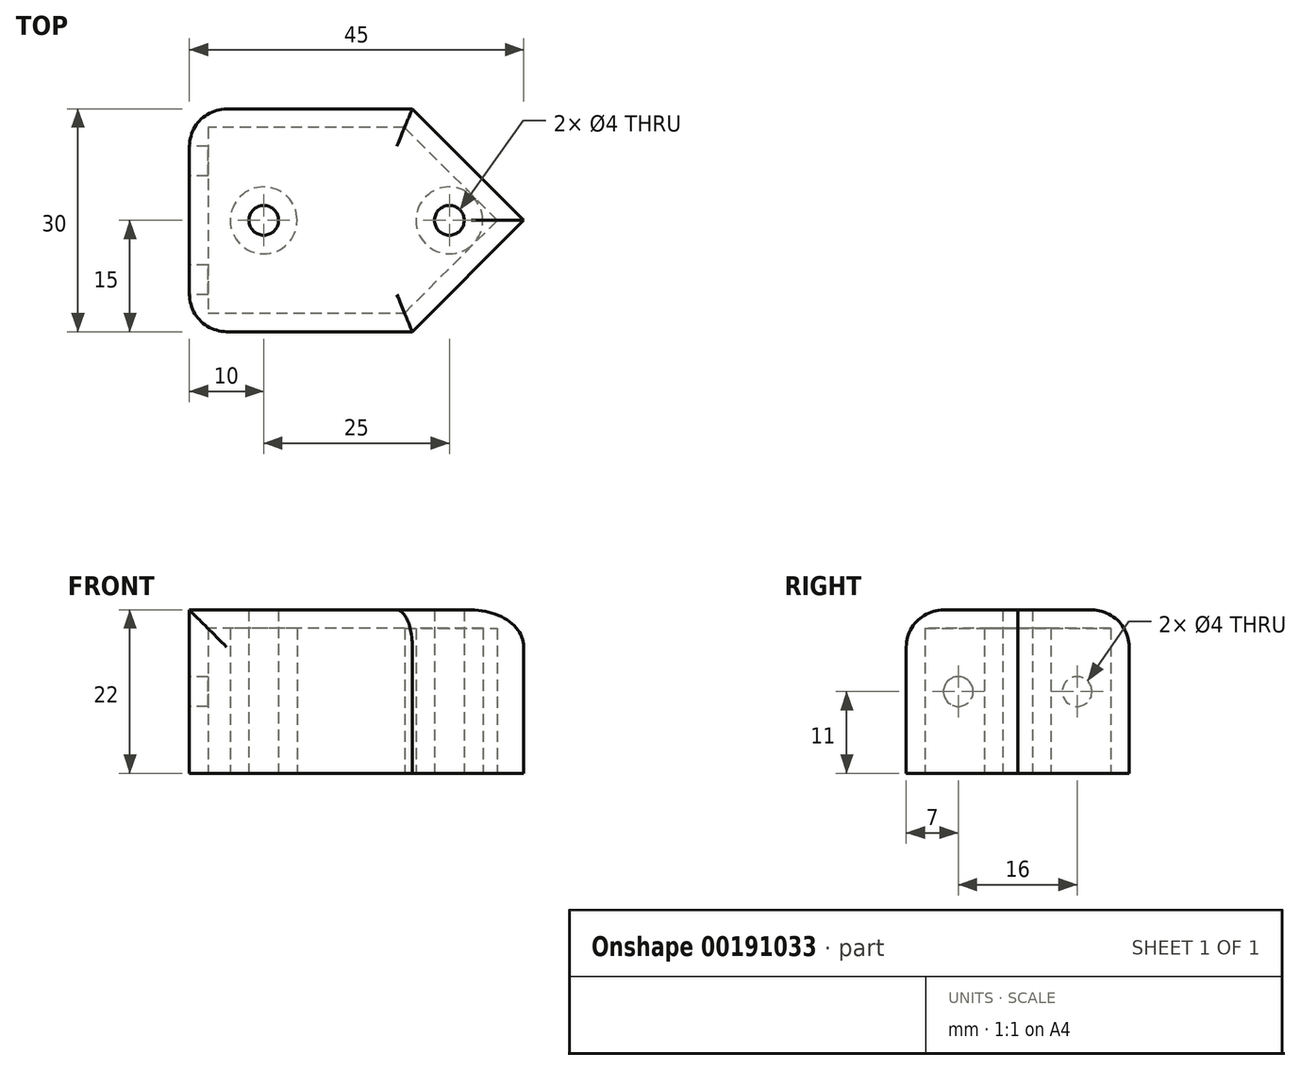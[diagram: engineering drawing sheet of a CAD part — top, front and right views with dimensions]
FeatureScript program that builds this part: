
annotation { "Feature Type Name" : "Feature", "Feature Type Description" : "" }
export const myFeature = defineFeature(function(context is Context, id is Id, definition is map)
    precondition{}
    {
        {
            var Q0;
            Q0=qCreatedBy(makeId("Top.planeOp"),FACE);
            var sketch = newSketch(context, id + "F0", { "sketchPlane" : qUnion([Q0])});
            skLineSegment(sketch, "E0", {"start": v(0, 0) * mm, "end": v(-15, 15) * mm});
            skLineSegment(sketch, "E1", {"start": v(-15, 15) * mm, "end": v(-45, 15) * mm});
            skLineSegment(sketch, "E2", {"start": v(-45, 15) * mm, "end": v(-45, -15) * mm});
            skLineSegment(sketch, "E3", {"start": v(-45, -15) * mm, "end": v(-15, -15) * mm});
            skLineSegment(sketch, "E4", {"start": v(-15, -15) * mm, "end": v(0, 0) * mm});
            skLineSegment(sketch, "E5", {"start": v(-45, 0) * mm, "end": v(0, 0) * mm, "construction": true});
            skLineSegment(sketch, "E6", {"start": v(-30, 15) * mm, "end": v(-30, -15) * mm, "construction": true});
            skPoint(sketch, "E7", {"position": v(-35, 0) * mm});
            skPoint(sketch, "E8", {"position": v(-10, 0) * mm});
            skSolve(sketch);
        }
        {
            var Q0;
            Q0=makeQuery(id+"F0.imprint","IMPRINT",FACE,{"disambiguationData":[TD([[makeQuery(id+"F0.imprint","IMPRINT",EDGE,{"derivedFrom":sQuery(id+"F0.wireOp",EDGE,"E0")}),1.0]])]});
            extrude(context, id + "F1", {"entities" : qUnion([Q0]), "depth" : 22 * mm});
        }
        {
            var Q0;
            Q0=sQuery(id+"F0.wireOp",VERTEX,"E7");
            var Q1;
            Q1=sQuery(id+"F0.wireOp",VERTEX,"E8");
            var Q2;
            Q2=makeQuery(id+"F1.opExtrude","SWEPT_BODY",BODY,{"disambiguationData":[OSD([sQuery(id+"F0.wireOp",EDGE,"E0"),sQuery(id+"F0.wireOp",EDGE,"E1"),sQuery(id+"F0.wireOp",EDGE,"E2"),sQuery(id+"F0.wireOp",EDGE,"E3"),sQuery(id+"F0.wireOp",EDGE,"E4")])]});
            hole(context, id + "F2", {"style" : HoleStyle.SIMPLE, "endStyle" : HoleEndStyle.THROUGH, "oppositeDirection" : true, "holeDiameter" : 4 * mm, "locations" : qUnion([Q0, Q1]), "scope" : qUnion([Q2]), "isTappedThrough" : true});
        }
        {
            var Q0;
            Q0=makeQuery(id+"F1.opExtrude","CAP_FACE",FACE,{"disambiguationData":[OSD([sQuery(id+"F0.wireOp",EDGE,"E0"),sQuery(id+"F0.wireOp",EDGE,"E1"),sQuery(id+"F0.wireOp",EDGE,"E2"),sQuery(id+"F0.wireOp",EDGE,"E3"),sQuery(id+"F0.wireOp",EDGE,"E4")])],"isStart":true});
            shell(context, id + "F3", {"entities" : qUnion([Q0]), "thickness" : 2.5 * mm});
        }
        {
            var Q0;
            Q0=makeQuery(id+"F1.opExtrude","SWEPT_FACE",FACE,{"disambiguationData":[OSD([sQuery(id+"F0.wireOp",EDGE,"E2")])]});
            var sketch = newSketch(context, id + "F4", { "sketchPlane" : qUnion([Q0])});
            skLineSegment(sketch, "E9", {"start": v(0, 22) * mm, "end": v(0, 0) * mm, "construction": true});
            skLineSegment(sketch, "E10", {"start": v(-15, 11) * mm, "end": v(15, 11) * mm, "construction": true});
            skPoint(sketch, "E11", {"position": v(-8, 11) * mm});
            skPoint(sketch, "E12.MirrorP", {"position": v(8, 11) * mm});
            skLineSegment(sketch, "E13.bottom", {"start": v(-15, 22) * mm, "end": v(15, 22) * mm});
            skLineSegment(sketch, "E13.top", {"start": v(-15, 0) * mm, "end": v(15, 0) * mm});
            skLineSegment(sketch, "E13.left", {"start": v(-15, 22) * mm, "end": v(-15, 0) * mm});
            skLineSegment(sketch, "E13.right", {"start": v(15, 22) * mm, "end": v(15, 0) * mm});
            skSolve(sketch);
        }
        {
            var Q0;
            Q0=sQuery(id+"F4.wireOp",VERTEX,"E11");
            var Q1;
            Q1=sQuery(id+"F4.wireOp",VERTEX,"E12.MirrorP");
            var Q2;
            Q2=makeQuery(id+"F1.opExtrude","SWEPT_BODY",BODY,{"disambiguationData":[OSD([sQuery(id+"F0.wireOp",EDGE,"E0"),sQuery(id+"F0.wireOp",EDGE,"E1"),sQuery(id+"F0.wireOp",EDGE,"E2"),sQuery(id+"F0.wireOp",EDGE,"E3"),sQuery(id+"F0.wireOp",EDGE,"E4")])]});
            hole(context, id + "F5", {"style" : HoleStyle.SIMPLE, "endStyle" : HoleEndStyle.BLIND, "holeDiameter" : 4 * mm, "holeDepth" : 6 * mm, "locations" : qUnion([Q0, Q1]), "scope" : qUnion([Q2])});
        }
        {
            var Q0;
            Q0=makeQuery(id+"F1.opExtrude","CAP_EDGE",EDGE,{"disambiguationData":[OSD([sQuery(id+"F0.wireOp",EDGE,"E3")])],"isStart":false});
            var Q1;
            Q1=makeQuery(id+"F1.opExtrude","CAP_EDGE",EDGE,{"disambiguationData":[OSD([sQuery(id+"F0.wireOp",EDGE,"E4")])],"isStart":false});
            var Q2;
            Q2=makeQuery(id+"F1.opExtrude","CAP_EDGE",EDGE,{"disambiguationData":[OSD([sQuery(id+"F0.wireOp",EDGE,"E0")])],"isStart":false});
            var Q3;
            Q3=makeQuery(id+"F1.opExtrude","CAP_EDGE",EDGE,{"disambiguationData":[OSD([sQuery(id+"F0.wireOp",EDGE,"E1")])],"isStart":false});
            var Q4;
            Q4=makeQuery(id+"F1.opExtrude","SWEPT_EDGE",EDGE,{"disambiguationData":[OSD([sQuery(id+"F0.wireOp",EDGE,"E1"),sQuery(id+"F0.wireOp",EDGE,"E2")])]});
            var Q5;
            Q5=makeQuery(id+"F1.opExtrude","SWEPT_EDGE",EDGE,{"disambiguationData":[OSD([sQuery(id+"F0.wireOp",EDGE,"E2"),sQuery(id+"F0.wireOp",EDGE,"E3")])]});
            fillet(context, id + "F6", {"entities" : qUnion([Q0, Q1, Q2, Q3, Q4, Q5]), "radius" : 5 * mm, "tangentPropagation" : true, "allowEdgeOverflow" : false});
        }
    });
